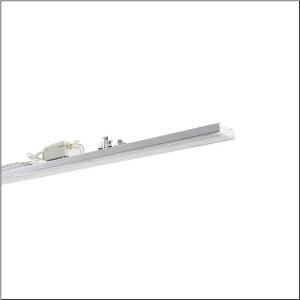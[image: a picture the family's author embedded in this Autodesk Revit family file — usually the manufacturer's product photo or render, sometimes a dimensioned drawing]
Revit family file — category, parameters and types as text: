
# Revit family: licross_r__21_recessed_ho_52tl12dv4l2m3s4_342f
name_source: partatom
category: Lighting Fixtures
units: mm (PartAtom-declared; Revit-internal decimal feet)

## family parameters
Cut with Voids When Loaded = No
Host = Face
Light Source = No
Part Type = Normal
Room Calculation Point = No
Round Connector Dimension = Use Diameter
Shared = No

## types (1)
- --- (1 x LED, 910 lm, 6.4 W, 4000K)
    Apparent Load = 6 VA
    CIE Flux Codes = 69 91 98 100 100
    Color Rendering = 80
    Color Temperature = 4000K
    Default Elevation = 1800 mm
    Description = Licross® 21 Recessed HO, luminaire insert, of sheet steel, galvanised, coil coated, white, length: 2.250mm, width: 66mm, height: 67mm, LED rated luminous flux: 22.710lm, light colour: 840, control gear: DALI 2, with plug, 6-pole, with phase selection, for trunking rail, 9 or 11-core, mains connection: 220..240V, AC, 50/60Hz, rated input power: 129W, for trunking rail, 9-/11-core, halogen-free wiring, for emergency light function, converter,control gear: single battery element, battery: LiFeP04, 9Ah, primary optical cover: cover, of PMMA, light emission: direct distribution, primary light characteristic: symmetric, protection rating (complete): IP40, insulation class (complete): insulation class I (protective earthing), certification: CE, UKCA, protection symbol: D if used in an environment without relevant dust loads with corresponding accessories, impact resistance: IK06, permissible ambient temperature for indoor applications: +5..+30°C, standard: EN 60598-2-22, LABS conformity tested according to VDMA 24364:2018-05, reducing of maximum allowable ambient temperature of 5°C with ceiling mounting, corresponds to IFS (International Featured Standards) requirements for safety and quality in the food industry, packaging unit: 1 piece
    Height = 58 mm
    Lamp = 1 x LED
    Lamp Light Flux = 910 lm
    Lamp Power = 6.4 W
    Lamp count = 1
    Length = 2250 mm
    Luminous efficacy = 142 lm/W
    Manufacturer = Siteco
    ModVariant = No
    Model = 52TL12DV4L2M3S4
    Mounting Place = Ceiling
    Mounting Type = Pendant
    Number of Poles = 1
    OnlyDefault = Yes
    Power Factor = 1
    Product Name = Licross® 21 Recessed HO
    Product group = luminaire insert
    ProductGroupID = 901
    Protection Class = Protection class I
    Protection Degree = IP 40
    RLX_Detail_Level = 1
    RLX_Emergency_Light_Flux = 0 lm
    RLX_Emergency_Type = 0
    RLX_Emergency_Type_DB = No
    RlxData = <blob elided: 29829 chars, md5=b49808d5>
    Socket = socket
    Standby Power = 0 W
    System Light Flux = 910 lm
    System Power = 6 W
    Type Comments = : emergency light operation: 3 h
    Type Image = l_1296930.jpg
    URL = http://relux.com
    VarID = @adj_039455
    Voltage = 0 V
    Weight = 0.00 kg
    Width = 66 mm

## geometry (parser evidence)
native form markers: Blend x4, Sweep x11
no freeform markers — native parametric forms only
